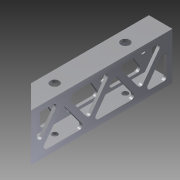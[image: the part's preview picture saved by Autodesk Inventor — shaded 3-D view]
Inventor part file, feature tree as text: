
AUTODESK INVENTOR PART (.ipt)
format: ipt  version: 2012 (Build 160160000, 160)  size: 279,552 bytes
history: native  units: in
note: dims shown in document units (in); Inventor stores cm internally (conversion verified against a paired STEP export)
features: extrude x6, sketch x5, mirror x1, fillet x1
ambient origin geometry x8: Origin, YZ Plane, XZ Plane, XY Plane, X Axis, Y Axis, Z Axis, Center Point
bodies: Solid1 (feature_tree)
feature tree (13):
  extrude  "Extrusion1"  Depth=1.0in
  sketch  "Sketch2"  dims[d2=0.125in d3=0.125in]
  extrude  "Extrusion2"  Depth=0.125in
  extrude  "Extrusion3"  Depth=0.125in
  mirror  "Mirror1"
  extrude  "Extrusion4"  TaperAngle=45.0deg  [1 undecoded]
  extrude  "Extrusion5"  Depth=0.5in
  extrude  "Extrusion6"  Depth=1.5in
  fillet  "Fillet1"  Radius=3.0in
  sketch  "Sketch1"  dims[d0=2.0in d1=1.0in]
  sketch  "Sketch3"  dims[d4=0.125in d5=0.125in]
  sketch  "Sketch4"  dims[d6=6.0in d7=0.0in d8=45.0deg]
  sketch  "Sketch5"  dims[d9=0.25in d10=0.5in d11=1.5in d12=3.0in d13=0.125in d14=0.0in d15=0.125in d16=0.0in d17=0.375in d18=1.0in d19=0.0in d20=0.2128in d21=0.4255in d22=0.4255in d23=0.4255in d24=0.4255in d25=0.125in d26=0.125in d27=0.125in d28=0.125in d29=0.125in d30=0.125in d31=0.125in d32=0.125in d33=0.125in d34=0.125in d35=0.25in d36=0.25in d37=0.25in d38=0.25in d39=0.125in d40=0.0in d41=0.2491in d42=0.4982in d43=0.4982in d44=0.4982in d45=0.4982in d46=0.125in d47=0.125in d48=0.125in d49=0.125in d50=0.125in d51=0.125in d52=0.125in d53=0.125in d54=0.125in d55=0.125in d56=0.25in d57=0.25in d58=0.25in d59=0.25in d60=0.125in d61=0.0in d62=0.125in]
note: 1 required parameter value undecoded (feature->parameter linkage not recoverable at this tier; creation-order binding heuristic only, values carry confidence <= 0.55)
